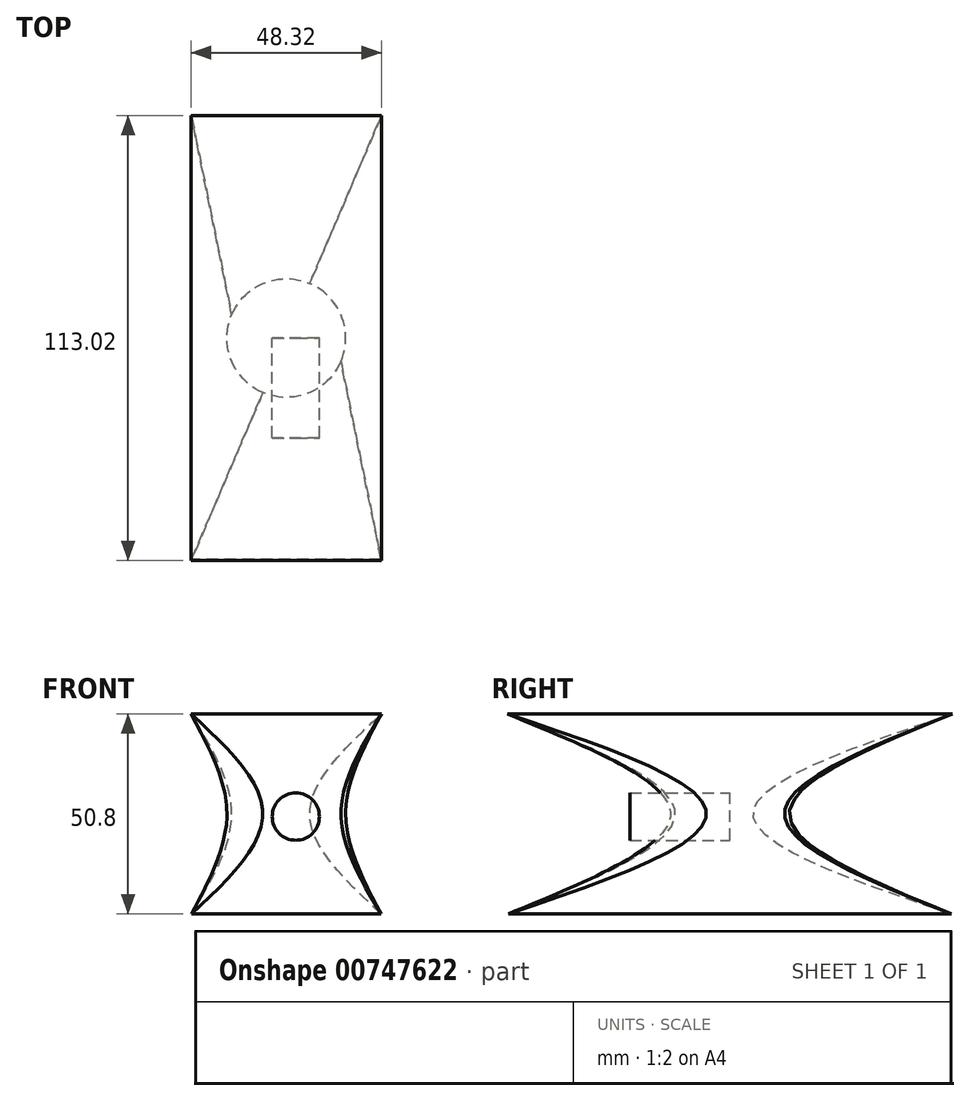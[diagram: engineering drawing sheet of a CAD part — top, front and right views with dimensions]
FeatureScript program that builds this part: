
annotation { "Feature Type Name" : "Feature", "Feature Type Description" : "" }
export const myFeature = defineFeature(function(context is Context, id is Id, definition is map)
    precondition{}
    {
        {
            var Q0;
            Q0=qCreatedBy(makeId("Top.planeOp"),FACE);
            var sketch = newSketch(context, id + "F0", { "sketchPlane" : qUnion([Q0])});
            skLineSegment(sketch, "E0.bottom", {"start": v(24.09, 56.26) * mm, "end": v(-24.09, 56.26) * mm});
            skLineSegment(sketch, "E0.top", {"start": v(24.09, -56.26) * mm, "end": v(-24.09, -56.26) * mm});
            skLineSegment(sketch, "E0.left", {"start": v(24.09, 56.26) * mm, "end": v(24.09, -56.26) * mm});
            skLineSegment(sketch, "E0.right", {"start": v(-24.09, 56.26) * mm, "end": v(-24.09, -56.26) * mm});
            skPoint(sketch, "E0.middle", {"position": v(0, 0) * mm});
            skSolve(sketch);
        }
        {
            var Q0;
            Q0=qCreatedBy(makeId("Top.planeOp"),FACE);
            cPlane(context, id + "F1", {"entities" : qUnion([Q0]), "cplaneType" : CPlaneType.OFFSET, "offset" : 25.4 * mm, "width" : 152.4 * mm, "height" : 152.4 * mm});
        }
        {
            var Q0;
            Q0=qCreatedBy(id+"F1.planeOp",FACE);
            var sketch = newSketch(context, id + "F2", { "sketchPlane" : qUnion([Q0])});
            skCircle(sketch, "E1", {"center": v(0, 0) * mm, "radius": 15.08 * mm});
            skSolve(sketch);
        }
        {
            var Q0;
            Q0=qCreatedBy(id+"F1.planeOp",FACE);
            cPlane(context, id + "F3", {"entities" : qUnion([Q0]), "cplaneType" : CPlaneType.OFFSET, "offset" : 25.4 * mm, "width" : 152.4 * mm, "height" : 152.4 * mm});
        }
        {
            var Q0;
            Q0=qCreatedBy(id+"F3.planeOp",FACE);
            var sketch = newSketch(context, id + "F4", { "sketchPlane" : qUnion([Q0])});
            skLineSegment(sketch, "E2.bottom", {"start": v(24.16, 56.5) * mm, "end": v(-24.16, 56.5) * mm});
            skLineSegment(sketch, "E2.top", {"start": v(24.16, -56.5) * mm, "end": v(-24.16, -56.5) * mm});
            skLineSegment(sketch, "E2.left", {"start": v(24.16, 56.5) * mm, "end": v(24.16, -56.5) * mm});
            skLineSegment(sketch, "E2.right", {"start": v(-24.16, 56.5) * mm, "end": v(-24.16, -56.5) * mm});
            skPoint(sketch, "E2.middle", {"position": v(0, 0) * mm});
            skSolve(sketch);
        }
        {
            var Q0;
            Q0=makeQuery(id+"F0.imprint","IMPRINT",FACE,{"disambiguationData":[TD([[makeQuery(id+"F0.imprint","IMPRINT",EDGE,{"derivedFrom":sQuery(id+"F0.wireOp",EDGE,"E0.bottom")}),1.0]])]});
            var Q1;
            Q1=makeQuery(id+"F2.imprint","IMPRINT",FACE,{"disambiguationData":[TD([[makeQuery(id+"F2.imprint","IMPRINT",EDGE,{"derivedFrom":sQuery(id+"F2.wireOp",EDGE,"E1")}),1.0]])]});
            var Q2;
            Q2=makeQuery(id+"F4.imprint","IMPRINT",FACE,{"disambiguationData":[TD([[makeQuery(id+"F4.imprint","IMPRINT",EDGE,{"derivedFrom":sQuery(id+"F4.wireOp",EDGE,"E2.bottom")}),1.0]])]});
            loft(context, id + "F5", {"sheetProfilesArray" : [{ "sheetProfileEntities" : qUnion([Q0]) }, { "sheetProfileEntities" : qUnion([Q1]) }, { "sheetProfileEntities" : qUnion([Q2]) }]});
        }
        {
            var Q0;
            Q0=qCreatedBy(makeId("Front.planeOp"),FACE);
            var sketch = newSketch(context, id + "F6", { "sketchPlane" : qUnion([Q0])});
            skCircle(sketch, "E3", {"center": v(2.41, 24.7) * mm, "radius": 6 * mm});
            skSolve(sketch);
        }
        {
            var Q0;
            Q0=makeQuery(id+"F6.imprint","IMPRINT",FACE,{"disambiguationData":[TD([[makeQuery(id+"F6.imprint","IMPRINT",EDGE,{"derivedFrom":sQuery(id+"F6.wireOp",EDGE,"E3")}),1.0]])]});
            extrude(context, id + "F7", {"entities" : qUnion([Q0]), "depth" : 25.4 * mm, "offsetDistance" : 25.4 * mm});
        }
    });
